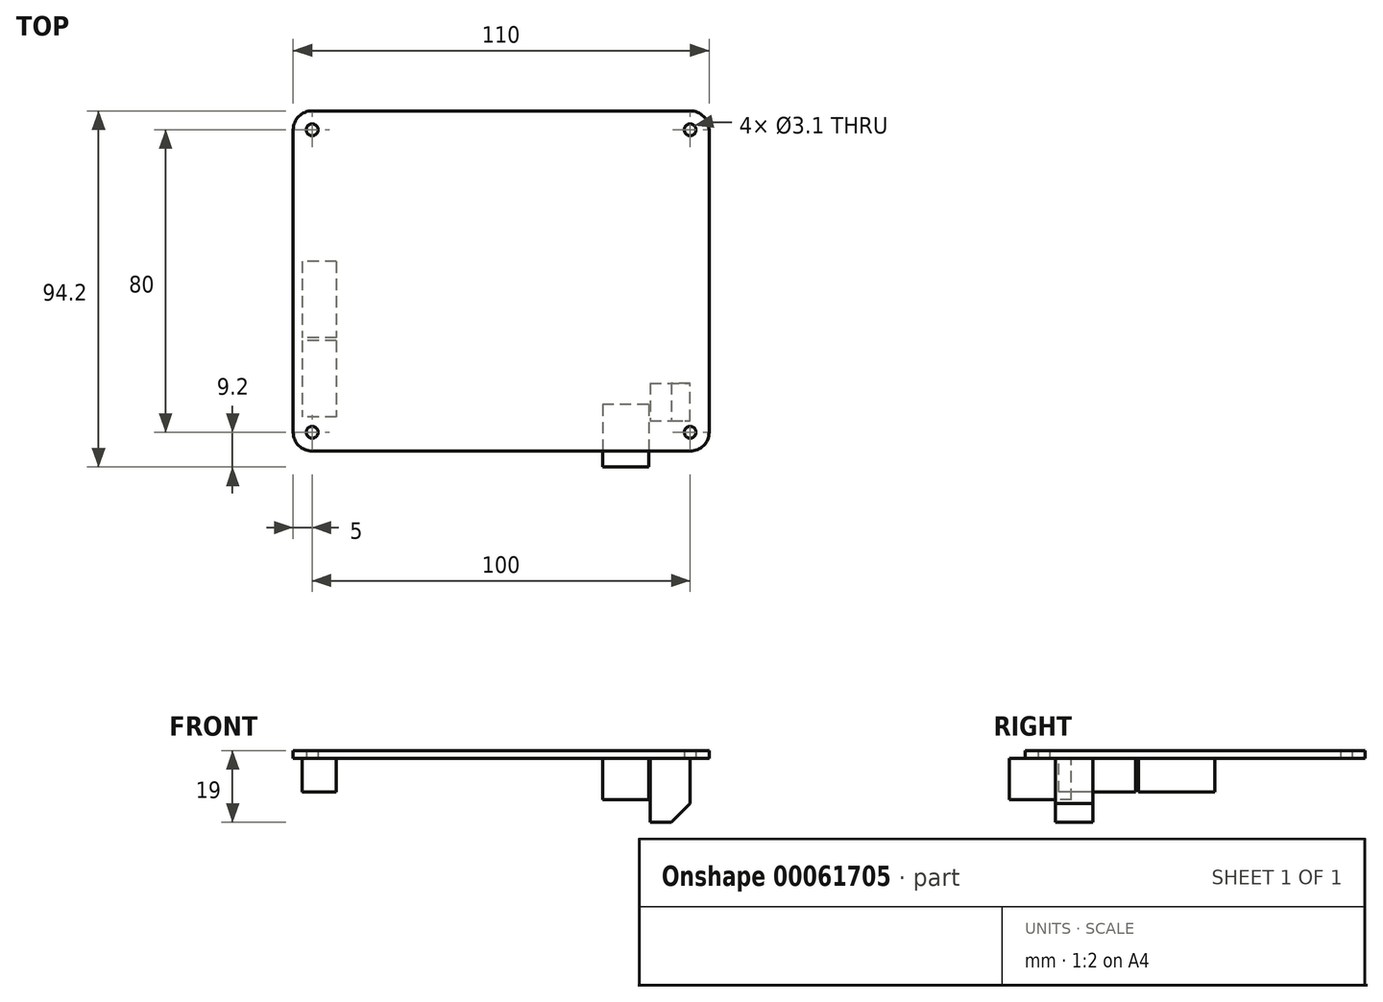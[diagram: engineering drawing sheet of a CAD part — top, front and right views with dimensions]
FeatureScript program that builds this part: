
annotation { "Feature Type Name" : "Feature", "Feature Type Description" : "" }
export const myFeature = defineFeature(function(context is Context, id is Id, definition is map)
    precondition{}
    {
        {
            var Q0;
            Q0=qCreatedBy(makeId("Top.planeOp"),FACE);
            var sketch = newSketch(context, id + "F0", { "sketchPlane" : qUnion([Q0])});
            skLineSegment(sketch, "E0.rect.bottom", {"start": v(-50, 40) * mm, "end": v(50, 40) * mm, "construction": true});
            skLineSegment(sketch, "E0.rect.top", {"start": v(-50, -40) * mm, "end": v(50, -40) * mm, "construction": true});
            skLineSegment(sketch, "E0.rect.left", {"start": v(-50, 40) * mm, "end": v(-50, -40) * mm, "construction": true});
            skLineSegment(sketch, "E0.rect.right", {"start": v(50, 40) * mm, "end": v(50, -40) * mm, "construction": true});
            skPoint(sketch, "E0.rect.middle", {"position": v(0, 0) * mm});
            skCircle(sketch, "E1", {"center": v(-50, 40) * mm, "radius": 1.55 * mm});
            skCircle(sketch, "E2", {"center": v(50, 40) * mm, "radius": 1.55 * mm});
            skCircle(sketch, "E3", {"center": v(50, -40) * mm, "radius": 1.55 * mm});
            skCircle(sketch, "E4", {"center": v(-50, -40) * mm, "radius": 1.55 * mm});
            skLineSegment(sketch, "E5.rect.bottom", {"start": v(-50, 45) * mm, "end": v(50, 45) * mm});
            skLineSegment(sketch, "E5.rect.top", {"start": v(-50, -45) * mm, "end": v(50, -45) * mm});
            skLineSegment(sketch, "E5.rect.left", {"start": v(-55, 40) * mm, "end": v(-55, -40) * mm});
            skLineSegment(sketch, "E5.rect.right", {"start": v(55, 40) * mm, "end": v(55, -40) * mm});
            skPoint(sketch, "E6.visualSharp", {"position": v(-55, 45) * mm});
            skArc(sketch, "E6.filletArc", {"start": v(-50, 45) * mm, "mid": v(-53.54, 43.54) * mm, "end": v(-55, 40) * mm});
            skPoint(sketch, "E7.visualSharp", {"position": v(55, 45) * mm});
            skArc(sketch, "E7.filletArc", {"start": v(55, 40) * mm, "mid": v(53.54, 43.54) * mm, "end": v(50, 45) * mm});
            skPoint(sketch, "E8.visualSharp", {"position": v(55, -45) * mm});
            skArc(sketch, "E8.filletArc", {"start": v(50, -45) * mm, "mid": v(53.54, -43.54) * mm, "end": v(55, -40) * mm});
            skPoint(sketch, "E9.visualSharp", {"position": v(-55, -45) * mm});
            skArc(sketch, "E9.filletArc", {"start": v(-55, -40) * mm, "mid": v(-53.54, -43.54) * mm, "end": v(-50, -45) * mm});
            skSolve(sketch);
        }
        {
            var Q0;
            Q0 = qSketchRegion(id + "F0", true);
            extrude(context, id + "F1", {"entities" : qUnion([Q0]), "depth" : 2 * mm});
        }
        {
            var Q0;
            Q0=qCreatedBy(makeId("Top.planeOp"),FACE);
            var sketch = newSketch(context, id + "F2", { "sketchPlane" : qUnion([Q0])});
            skLineSegment(sketch, "E10.bottom", {"start": v(39.4, -27) * mm, "end": v(55, -27) * mm});
            skLineSegment(sketch, "E10.top", {"start": v(39.4, -37) * mm, "end": v(55, -37) * mm});
            skLineSegment(sketch, "E10.left", {"start": v(39.4, -27) * mm, "end": v(39.4, -37) * mm});
            skLineSegment(sketch, "E10.right", {"start": v(55, -27) * mm, "end": v(55, -37) * mm});
            skLineSegment(sketch, "E11.bottom", {"start": v(39, -32.7) * mm, "end": v(26.8, -32.7) * mm});
            skLineSegment(sketch, "E11.top", {"start": v(39, -49.2) * mm, "end": v(26.8, -49.2) * mm});
            skLineSegment(sketch, "E11.left", {"start": v(39, -32.7) * mm, "end": v(39, -49.2) * mm});
            skLineSegment(sketch, "E11.right", {"start": v(26.8, -32.7) * mm, "end": v(26.8, -49.2) * mm});
            skLineSegment(sketch, "E12.bottom", {"start": v(-43.6, 5.2) * mm, "end": v(-52.6, 5.2) * mm});
            skLineSegment(sketch, "E12.top", {"start": v(-43.6, -15) * mm, "end": v(-52.6, -15) * mm});
            skLineSegment(sketch, "E12.left", {"start": v(-43.6, 5.2) * mm, "end": v(-43.6, -15) * mm});
            skLineSegment(sketch, "E12.right", {"start": v(-52.6, 5.2) * mm, "end": v(-52.6, -15) * mm});
            skLineSegment(sketch, "E13.bottom", {"start": v(-43.6, -15.8) * mm, "end": v(-52.6, -15.8) * mm});
            skLineSegment(sketch, "E13.top", {"start": v(-43.6, -36) * mm, "end": v(-52.6, -36) * mm});
            skLineSegment(sketch, "E13.left", {"start": v(-43.6, -15.8) * mm, "end": v(-43.6, -36) * mm});
            skLineSegment(sketch, "E13.right", {"start": v(-52.6, -15.8) * mm, "end": v(-52.6, -36) * mm});
            skLineSegment(sketch, "E14.0", {"start": v(-50, -45) * mm, "end": v(50, -45) * mm, "construction": true});
            skArc(sketch, "E14.1", {"start": v(50, -45) * mm, "mid": v(53.54, -43.54) * mm, "end": v(55, -40) * mm, "construction": true});
            skLineSegment(sketch, "E14.2", {"start": v(55, 40) * mm, "end": v(55, -40) * mm, "construction": true});
            skArc(sketch, "E14.3", {"start": v(55, 40) * mm, "mid": v(53.54, 43.54) * mm, "end": v(50, 45) * mm, "construction": true});
            skLineSegment(sketch, "E14.4", {"start": v(-50, 45) * mm, "end": v(50, 45) * mm, "construction": true});
            skArc(sketch, "E14.5", {"start": v(-50, 45) * mm, "mid": v(-53.54, 43.54) * mm, "end": v(-55, 40) * mm, "construction": true});
            skLineSegment(sketch, "E14.6", {"start": v(-55, 40) * mm, "end": v(-55, -40) * mm, "construction": true});
            skArc(sketch, "E14.7", {"start": v(-55, -40) * mm, "mid": v(-53.54, -43.54) * mm, "end": v(-50, -45) * mm, "construction": true});
            skLineSegment(sketch, "E15", {"start": v(50, -37) * mm, "end": v(50, -27) * mm});
            skSolve(sketch);
        }
        {
            var Q0;
            {var subQ0=sQuery(id+"F2.wireOp",EDGE,"E11.bottom");Q0=makeQuery(id+"F2.imprint","IMPRINT",FACE,{"disambiguationData":[TD([[makeQuery(id+"F2.imprint","IMPRINT",EDGE,{"derivedFrom":subQ0}),1.0]])]});}
            var Q1;
            {var subQ0=sQuery(id+"F2.wireOp",EDGE,"E11.top");Q1=makeQuery(id+"F2.imprint","IMPRINT",FACE,{"disambiguationData":[TD([[makeQuery(id+"F2.imprint","IMPRINT",EDGE,{"derivedFrom":subQ0}),-1.0]])]});}
            extrude(context, id + "F3", {"entities" : qUnion([Q0, Q1]), "operationType" : NewBodyOperationType.ADD, "oppositeDirection" : true, "depth" : 11 * mm});
        }
        {
            var Q0;
            {var subQ0=sQuery(id+"F2.wireOp",EDGE,"E10.left");Q0=makeQuery(id+"F2.imprint","IMPRINT",FACE,{"disambiguationData":[TD([[makeQuery(id+"F2.imprint","IMPRINT",EDGE,{"derivedFrom":subQ0}),1.0]])]});}
            extrude(context, id + "F4", {"entities" : qUnion([Q0]), "operationType" : NewBodyOperationType.ADD, "oppositeDirection" : true, "depth" : 17 * mm});
        }
        {
            var Q0;
            Q0=makeQuery(id+"F4.opExtrude","CAP_EDGE",EDGE,{"disambiguationData":[OSD([sQuery(id+"F2.wireOp",EDGE,"E15")])],"isStart":false});
            chamfer(context, id + "F5", {"entities" : qUnion([Q0]), "width" : 5 * mm, "tangentPropagation" : true});
        }
        {
            var Q0;
            Q0=makeQuery(id+"F2.imprint","IMPRINT",FACE,{"disambiguationData":[TD([[makeQuery(id+"F2.imprint","IMPRINT",EDGE,{"derivedFrom":sQuery(id+"F2.wireOp",EDGE,"E13.bottom")}),1.0]])]});
            var Q1;
            Q1=makeQuery(id+"F2.imprint","IMPRINT",FACE,{"disambiguationData":[TD([[makeQuery(id+"F2.imprint","IMPRINT",EDGE,{"derivedFrom":sQuery(id+"F2.wireOp",EDGE,"E12.bottom")}),1.0]])]});
            extrude(context, id + "F6", {"entities" : qUnion([Q0, Q1]), "operationType" : NewBodyOperationType.ADD, "oppositeDirection" : true, "depth" : 9 * mm});
        }
    });
